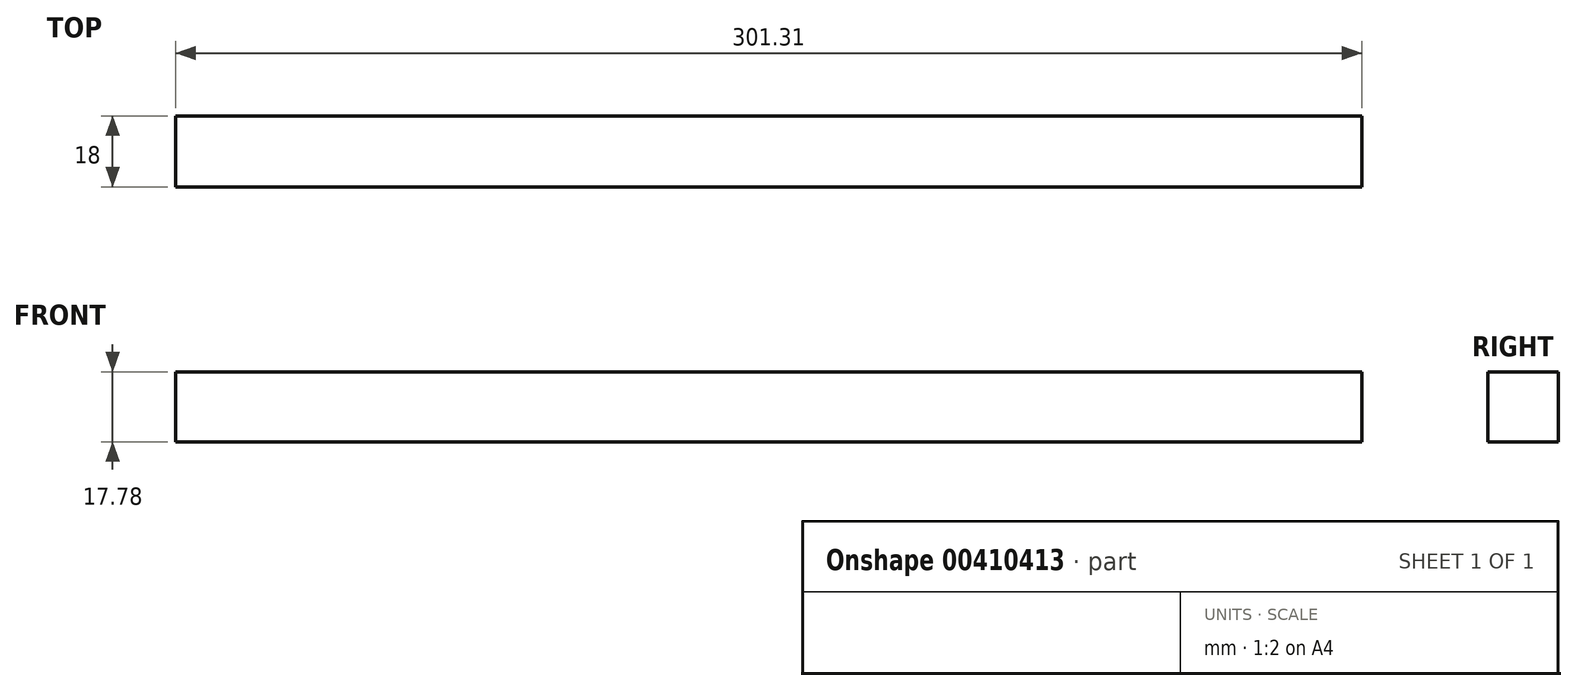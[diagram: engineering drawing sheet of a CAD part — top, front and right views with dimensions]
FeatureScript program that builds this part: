
annotation { "Feature Type Name" : "Feature", "Feature Type Description" : "" }
export const myFeature = defineFeature(function(context is Context, id is Id, definition is map)
    precondition{}
    {
        {
            var Q0;
            Q0=qCreatedBy(makeId("Front.planeOp"),FACE);
            var sketch = newSketch(context, id + "F0", { "sketchPlane" : qUnion([Q0])});
            skLineSegment(sketch, "E0.bottom", {"start": v(-150.86, 0) * mm, "end": v(150.45, 0) * mm});
            skLineSegment(sketch, "E0.top", {"start": v(-150.86, 17.78) * mm, "end": v(150.45, 17.78) * mm});
            skLineSegment(sketch, "E0.left", {"start": v(-150.86, 0) * mm, "end": v(-150.86, 17.78) * mm});
            skLineSegment(sketch, "E0.right", {"start": v(150.45, 0) * mm, "end": v(150.45, 17.78) * mm});
            skLineSegment(sketch, "E1", {"start": v(-62.55, 17.78) * mm, "end": v(62.55, 17.78) * mm});
            skSolve(sketch);
        }
        {
            var Q0;
            Q0 = qSketchRegion(id + "F0", true);
            extrude(context, id + "F1", {"entities" : qUnion([Q0]), "oppositeDirection" : true, "depth" : 18 * mm});
        }
    });
